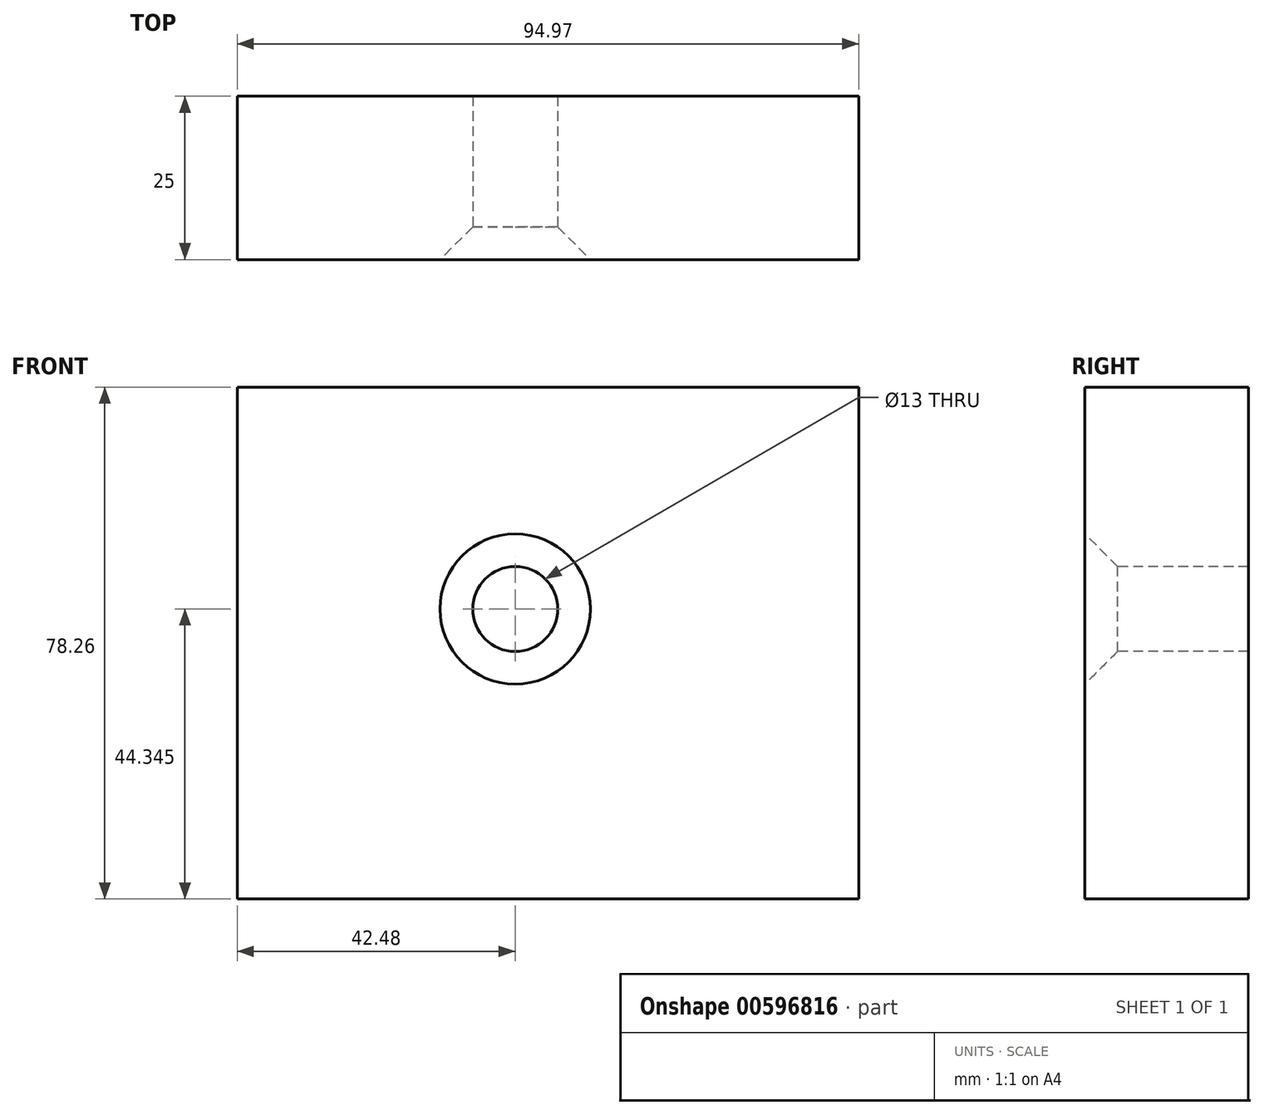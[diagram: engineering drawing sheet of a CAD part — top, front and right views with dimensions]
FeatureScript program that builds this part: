
annotation { "Feature Type Name" : "Feature", "Feature Type Description" : "" }
export const myFeature = defineFeature(function(context is Context, id is Id, definition is map)
    precondition{}
    {
        {
            var Q0;
            Q0=qCreatedBy(makeId("Front.planeOp"),FACE);
            var sketch = newSketch(context, id + "F0", { "sketchPlane" : qUnion([Q0])});
            skLineSegment(sketch, "E0.bottom", {"start": v(-106.55, 41.9) * mm, "end": v(-11.58, 41.9) * mm});
            skLineSegment(sketch, "E0.top", {"start": v(-106.55, -36.35) * mm, "end": v(-11.58, -36.35) * mm});
            skLineSegment(sketch, "E0.left", {"start": v(-106.55, 41.9) * mm, "end": v(-106.55, -36.35) * mm});
            skLineSegment(sketch, "E0.right", {"start": v(-11.58, 41.9) * mm, "end": v(-11.58, -36.35) * mm});
            skSolve(sketch);
        }
        {
            var Q0;
            Q0 = qSketchRegion(id + "F0", true);
            extrude(context, id + "F1", {"entities" : qUnion([Q0]), "depth" : 25 * mm, "offsetDistance" : 25 * mm});
        }
        {
            var Q0;
            Q0=makeQuery(id+"F1.opExtrude","CAP_FACE",FACE,{"disambiguationData":[OSD([sQuery(id+"F0.wireOp",EDGE,"E0.bottom"),sQuery(id+"F0.wireOp",EDGE,"E0.top"),sQuery(id+"F0.wireOp",EDGE,"E0.left"),sQuery(id+"F0.wireOp",EDGE,"E0.right")])],"isStart":false});
            var sketch = newSketch(context, id + "F2", { "sketchPlane" : qUnion([Q0])});
            skPoint(sketch, "E1", {"position": v(-64.07, 8) * mm});
            skSolve(sketch);
        }
        {
            var Q0;
            Q0=sQuery(id+"F2.wireOp",VERTEX,"E1");
            var Q1;
            Q1=makeQuery(id+"F1.opExtrude","SWEPT_BODY",BODY,{"disambiguationData":[OSD([sQuery(id+"F0.wireOp",EDGE,"E0.bottom"),sQuery(id+"F0.wireOp",EDGE,"E0.top"),sQuery(id+"F0.wireOp",EDGE,"E0.left"),sQuery(id+"F0.wireOp",EDGE,"E0.right")])]});
            hole(context, id + "F3", {"style" : HoleStyle.C_SINK, "endStyle" : HoleEndStyle.THROUGH, "holeDiameter" : 13 * mm, "cSinkDiameter" : 23 * mm, "cSinkAngle" : 90 * degree, "majorDiameter" : 5 * mm, "isTappedThrough" : true, "tappedDepth" : 12 * mm, "tapClearance" : 3, "startFromSketch" : true, "locations" : qUnion([Q0]), "scope" : qUnion([Q1])});
        }
    });
